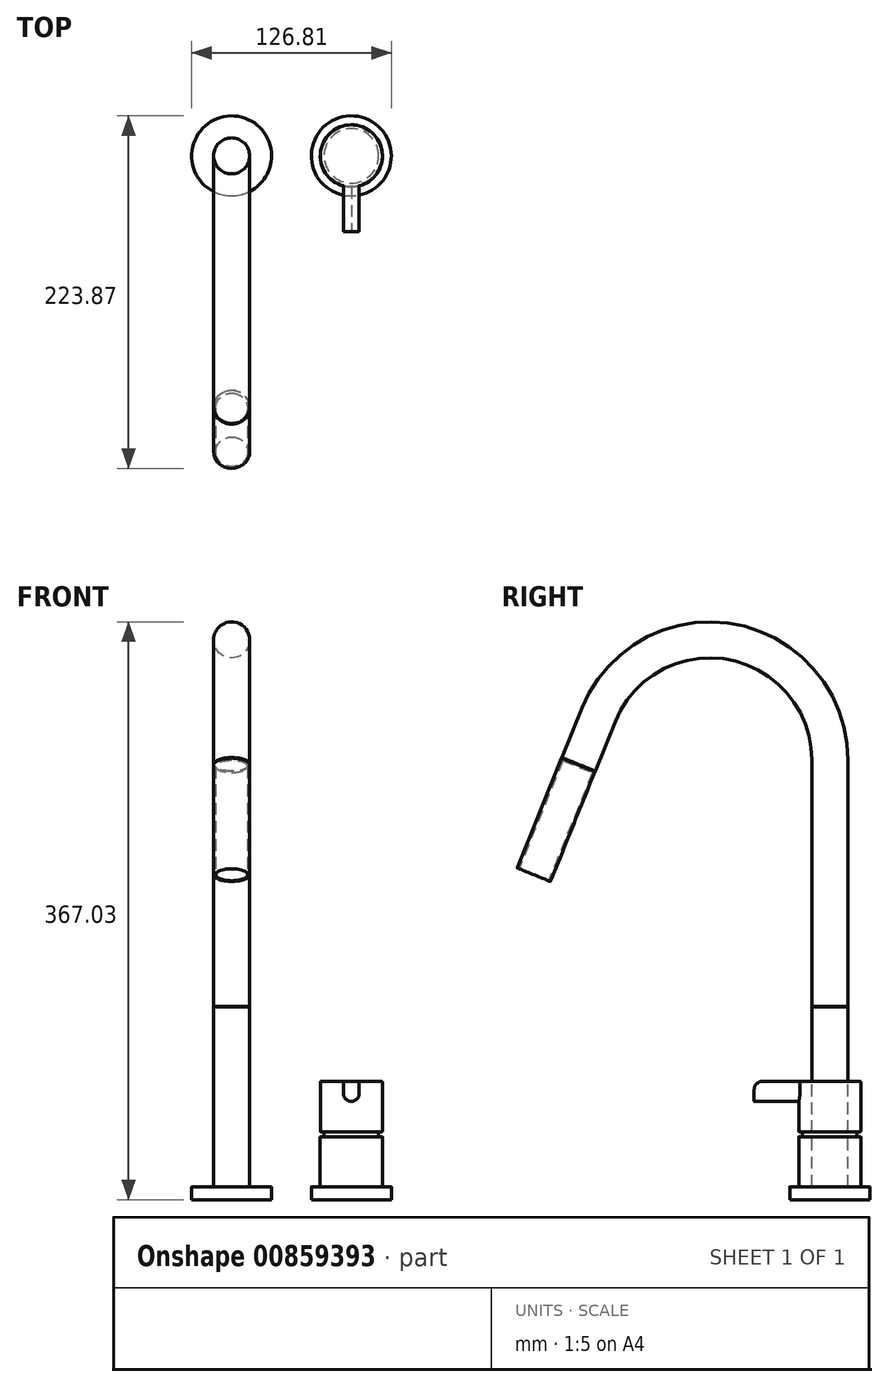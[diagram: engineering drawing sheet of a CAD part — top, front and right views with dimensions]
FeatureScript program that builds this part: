
annotation { "Feature Type Name" : "Feature", "Feature Type Description" : "" }
export const myFeature = defineFeature(function(context is Context, id is Id, definition is map)
    precondition{}
    {
        {
            var Q0;
            Q0=qCreatedBy(makeId("Top.planeOp"),FACE);
            var sketch = newSketch(context, id + "F0", { "sketchPlane" : qUnion([Q0])});
            skCircle(sketch, "E0", {"center": v(0, 0) * mm, "radius": 25.4 * mm});
            skSolve(sketch);
        }
        {
            var Q0;
            Q0=makeQuery(id+"F0.imprint","IMPRINT",FACE,{"disambiguationData":[TD([[makeQuery(id+"F0.imprint","IMPRINT",EDGE,{"derivedFrom":sQuery(id+"F0.wireOp",EDGE,"E0")}),1.0]])]});
            extrude(context, id + "F1", {"entities" : qUnion([Q0]), "depth" : 8.25 * mm, "offsetDistance" : 25.4 * mm});
        }
        {
            var Q0;
            Q0=qCreatedBy(makeId("Right.planeOp"),FACE);
            var sketch = newSketch(context, id + "F2", { "sketchPlane" : qUnion([Q0])});
            skLineSegment(sketch, "E1", {"start": v(0, 0) * mm, "end": v(0, 279.4) * mm});
            skArc(sketch, "E2", {"start": v(0, 279.4) * mm, "mid": v(-61.63, 354.2) * mm, "end": v(-146.83, 308) * mm});
            skLineSegment(sketch, "E3", {"start": v(-76.2, 279.4) * mm, "end": v(-173.41, 318.76) * mm, "construction": true});
            skLineSegment(sketch, "E4", {"start": v(-146.83, 308) * mm, "end": v(-187.97, 206.4) * mm});
            skSolve(sketch);
        }
        {
            var Q0;
            Q0=qCreatedBy(makeId("Top.planeOp"),FACE);
            var sketch = newSketch(context, id + "F3", { "sketchPlane" : qUnion([Q0])});
            skCircle(sketch, "E5", {"center": v(0, 0) * mm, "radius": 11.43 * mm});
            skSolve(sketch);
        }
        {
            var Q0;
            Q0=makeQuery(id+"F3.imprint","IMPRINT",FACE,{"disambiguationData":[TD([[makeQuery(id+"F3.imprint","IMPRINT",EDGE,{"derivedFrom":sQuery(id+"F3.wireOp",EDGE,"E5")}),1.0]])]});
            var Q1;
            Q1=sQuery(id+"F2.wireOp",EDGE,"E1");
            var Q2;
            Q2=sQuery(id+"F2.wireOp",EDGE,"E2");
            var Q3;
            Q3=sQuery(id+"F2.wireOp",EDGE,"E4");
            sweep(context, id + "F4", {"operationType" : NewBodyOperationType.ADD, "profiles" : qUnion([Q0]), "path" : qUnion([Q1, Q2, Q3])});
        }
        {
            var Q0;
            Q0=qCreatedBy(makeId("Top.planeOp"),FACE);
            var sketch = newSketch(context, id + "F5", { "sketchPlane" : qUnion([Q0])});
            skCircle(sketch, "E6", {"center": v(76.01, 0) * mm, "radius": 25.4 * mm});
            skSolve(sketch);
        }
        {
            var Q0;
            Q0 = qSketchRegion(id + "F5", true);
            extrude(context, id + "F6", {"entities" : qUnion([Q0]), "depth" : 8.25 * mm, "offsetDistance" : 25.4 * mm});
        }
        {
            var Q0;
            Q0=makeQuery(id+"F6.opExtrude","CAP_FACE",FACE,{"disambiguationData":[OSD([sQuery(id+"F5.wireOp",EDGE,"E6")])],"isStart":false});
            var sketch = newSketch(context, id + "F7", { "sketchPlane" : qUnion([Q0])});
            skCircle(sketch, "E7", {"center": v(76.01, 0) * mm, "radius": 19.74 * mm});
            skSolve(sketch);
        }
        {
            var Q0;
            Q0 = qSketchRegion(id + "F7", true);
            extrude(context, id + "F8", {"entities" : qUnion([Q0]), "operationType" : NewBodyOperationType.ADD, "depth" : 31.75 * mm, "offsetDistance" : 25.4 * mm});
        }
        {
            var Q0;
            Q0=makeQuery(id+"F8.opExtrude","CAP_FACE",FACE,{"disambiguationData":[OSD([sQuery(id+"F7.wireOp",EDGE,"E7")])],"isStart":false});
            var sketch = newSketch(context, id + "F9", { "sketchPlane" : qUnion([Q0])});
            skCircle(sketch, "E8", {"center": v(76.01, 0) * mm, "radius": 17.3 * mm});
            skSolve(sketch);
        }
        {
            var Q0;
            Q0 = qSketchRegion(id + "F9", true);
            extrude(context, id + "F10", {"entities" : qUnion([Q0]), "operationType" : NewBodyOperationType.ADD, "depth" : 3.17 * mm, "offsetDistance" : 25.4 * mm});
        }
        {
            var Q0;
            Q0=makeQuery(id+"F10.opExtrude","CAP_FACE",FACE,{"disambiguationData":[OSD([sQuery(id+"F9.wireOp",EDGE,"E8")])],"isStart":false});
            var sketch = newSketch(context, id + "F11", { "sketchPlane" : qUnion([Q0])});
            skCircle(sketch, "E9", {"center": v(76.01, 0) * mm, "radius": 19.69 * mm});
            skSolve(sketch);
        }
        {
            var Q0;
            Q0 = qSketchRegion(id + "F11", true);
            extrude(context, id + "F12", {"entities" : qUnion([Q0]), "operationType" : NewBodyOperationType.ADD, "depth" : 31.88 * mm, "offsetDistance" : 25.4 * mm});
        }
        {
            var Q0;
            Q0=makeQuery(id+"F12.opExtrude","CAP_FACE",FACE,{"disambiguationData":[OSD([sQuery(id+"F11.wireOp",EDGE,"E9")])],"isStart":false});
            var sketch = newSketch(context, id + "F13", { "sketchPlane" : qUnion([Q0])});
            skArc(sketch, "E10", {"start": v(70.99, 0) * mm, "mid": v(76.01, 5.02) * mm, "end": v(81.03, 0) * mm});
            skLineSegment(sketch, "E11", {"start": v(81.03, 0) * mm, "end": v(81.03, -48.02) * mm});
            skLineSegment(sketch, "E12", {"start": v(81.03, -48.02) * mm, "end": v(70.99, -48.02) * mm});
            skLineSegment(sketch, "E13", {"start": v(70.99, -48.02) * mm, "end": v(70.99, 0) * mm});
            skSolve(sketch);
        }
        {
            var Q0;
            Q0 = qSketchRegion(id + "F13", true);
            extrude(context, id + "F14", {"entities" : qUnion([Q0]), "operationType" : NewBodyOperationType.ADD, "oppositeDirection" : true, "depth" : 12.7 * mm, "offsetDistance" : 25.4 * mm});
        }
        {
            var Q0;
            Q0=makeQuery(id+"F14.opExtrude","CAP_EDGE",EDGE,{"disambiguationData":[OSD([sQuery(id+"F13.wireOp",EDGE,"E11")])],"isStart":false});
            var Q1;
            Q1=makeQuery(id+"F14.opExtrude","CAP_EDGE",EDGE,{"disambiguationData":[OSD([sQuery(id+"F13.wireOp",EDGE,"E13")])],"isStart":false});
            var Q2;
            Q2=makeQuery(id+"F14.opExtrude","CAP_EDGE",EDGE,{"disambiguationData":[OSD([sQuery(id+"F13.wireOp",EDGE,"E12")])],"isStart":true});
            fillet(context, id + "F15", {"entities" : qUnion([Q0, Q1, Q2]), "radius" : 5.08 * mm, "tangentPropagation" : true, "allowEdgeOverflow" : false});
        }
        {
            var Q0;
            Q0=makeQuery(id+"F6.opExtrude","CAP_EDGE",EDGE,{"disambiguationData":[OSD([sQuery(id+"F5.wireOp",EDGE,"E6")])],"isStart":false});
            var Q1;
            Q1=makeQuery(id+"F1.opExtrude","CAP_EDGE",EDGE,{"disambiguationData":[OSD([sQuery(id+"F0.wireOp",EDGE,"E0")])],"isStart":false});
            var Q2;
            Q2=makeQuery(id+"F8.opExtrude","CAP_EDGE",EDGE,{"disambiguationData":[OSD([sQuery(id+"F7.wireOp",EDGE,"E7")])],"isStart":false});
            var Q3;
            Q3=makeQuery(id+"F12.opExtrude","CAP_EDGE",EDGE,{"disambiguationData":[OSD([sQuery(id+"F11.wireOp",EDGE,"E9")])],"isStart":true});
            var Q4;
            Q4=makeQuery(id+"F12.opExtrude","CAP_EDGE",EDGE,{"disambiguationData":[OSD([sQuery(id+"F11.wireOp",EDGE,"E9")])],"isStart":false});
            var Q5;
            Q5=makeQuery(id+"F14.opExtrude","CAP_EDGE",EDGE,{"disambiguationData":[OSD([sQuery(id+"F13.wireOp",EDGE,"E13")])],"isStart":true});
            var Q6;
            Q6=makeQuery(id+"F15.opFillet","BLEND_EDGE",EDGE,{"blendedFrom":[makeQuery(id+"F14.opExtrude","CAP_EDGE",EDGE,{"disambiguationData":[OSD([sQuery(id+"F13.wireOp",EDGE,"E12")])],"isStart":true}),makeQuery(id+"F14.opExtrude","SWEPT_FACE",FACE,{"disambiguationData":[OSD([sQuery(id+"F13.wireOp",EDGE,"E11")])]})],"blendedInto":[makeQuery(id+"F14.opExtrude","SWEPT_FACE",FACE,{"disambiguationData":[OSD([sQuery(id+"F13.wireOp",EDGE,"E11")])]})]});
            var Q7;
            Q7=makeQuery(id+"F14.opExtrude","CAP_EDGE",EDGE,{"disambiguationData":[OSD([sQuery(id+"F13.wireOp",EDGE,"E11")])],"isStart":true});
            fillet(context, id + "F16", {"entities" : qUnion([Q0, Q1, Q2, Q3, Q4, Q5, Q6, Q7]), "radius" : 0.32 * mm, "tangentPropagation" : true, "allowEdgeOverflow" : false});
        }
        {
            var Q0;
            Q0=makeQuery(id+"F4.opSweep","CAP_EDGE",EDGE,{"disambiguationData":[OSD([sQuery(id+"F2.wireOp",VERTEX,"E4.end"),sQuery(id+"F3.wireOp",EDGE,"E5")])],"isStart":false});
            fillet(context, id + "F17", {"entities" : qUnion([Q0]), "radius" : 0.32 * mm, "tangentPropagation" : true, "allowEdgeOverflow" : false});
        }
        {
            var Q0;
            Q0=qCreatedBy(makeId("Right.planeOp"),FACE);
            var sketch = newSketch(context, id + "F18", { "sketchPlane" : qUnion([Q0])});
            skLineSegment(sketch, "E14.bottom", {"start": v(18.5, 122.57) * mm, "end": v(-12.47, 122.57) * mm});
            skLineSegment(sketch, "E14.top", {"start": v(18.5, 122.6) * mm, "end": v(-12.47, 122.6) * mm});
            skLineSegment(sketch, "E14.left", {"start": v(18.5, 122.6) * mm, "end": v(18.5, 122.57) * mm});
            skLineSegment(sketch, "E14.right", {"start": v(-12.47, 122.6) * mm, "end": v(-12.47, 122.57) * mm});
            skLineSegment(sketch, "E15", {"start": v(-178.29, 283.88) * mm, "end": v(-139.78, 268.41) * mm});
            skLineSegment(sketch, "E16", {"start": v(-139.78, 268.41) * mm, "end": v(-139.83, 268.3) * mm});
            skLineSegment(sketch, "E17", {"start": v(-178.33, 283.76) * mm, "end": v(-178.29, 283.88) * mm});
            skLineSegment(sketch, "E18", {"start": v(-178.33, 283.76) * mm, "end": v(-139.83, 268.3) * mm});
            skSolve(sketch);
        }
        {
            var Q0;
            Q0 = qSketchRegion(id + "F18", true);
            extrude(context, id + "F19", {"entities" : qUnion([Q0]), "operationType" : NewBodyOperationType.REMOVE, "endBound" : BoundingType.THROUGH_ALL, "oppositeDirection" : true, "depth" : 50.8 * mm, "offsetDistance" : 25.4 * mm, "hasSecondDirection" : true, "secondDirectionBound" : SecondDirectionBoundingType.THROUGH_ALL, "secondDirectionOppositeDirection" : false, "secondDirectionDepth" : 25.4 * mm});
        }
        {
            var Q0;
            Q0=makeQuery(id+"F4.opSweep","CAP_FACE",FACE,{"disambiguationData":[OSD([sQuery(id+"F2.wireOp",VERTEX,"E4.end"),sQuery(id+"F3.wireOp",EDGE,"E5")])],"isStart":false});
            shell(context, id + "F20", {"entities" : qUnion([Q0]), "thickness" : 1.27 * mm});
        }
        {
            var Q0;
            Q0=makeQuery(id+"F19.boolean.opBoolean","INTERSECT",EDGE,{"derivedFrom":[makeQuery(id+"F4.opSweep","SWEPT_FACE",FACE,{"disambiguationData":[OSD([sQuery(id+"F2.wireOp",EDGE,"E4"),sQuery(id+"F3.wireOp",EDGE,"E5")])]}),makeQuery(id+"F19.opExtrude","SWEPT_FACE",FACE,{"disambiguationData":[OSD([sQuery(id+"F18.wireOp",EDGE,"E15")])]})]});
            var Q1;
            Q1=makeQuery(id+"F19.boolean.opBoolean","INTERSECT",EDGE,{"derivedFrom":[makeQuery(id+"F4.opSweep","SWEPT_FACE",FACE,{"disambiguationData":[OSD([sQuery(id+"F2.wireOp",EDGE,"E4"),sQuery(id+"F3.wireOp",EDGE,"E5")])]}),makeQuery(id+"F19.opExtrude","SWEPT_FACE",FACE,{"disambiguationData":[OSD([sQuery(id+"F18.wireOp",EDGE,"E18")])]})]});
            var Q2;
            Q2=makeQuery(id+"F19.boolean.opBoolean","INTERSECT",EDGE,{"derivedFrom":[makeQuery(id+"F4.opSweep","SWEPT_FACE",FACE,{"disambiguationData":[OSD([sQuery(id+"F2.wireOp",EDGE,"E1"),sQuery(id+"F3.wireOp",EDGE,"E5")])]}),makeQuery(id+"F19.opExtrude","SWEPT_FACE",FACE,{"disambiguationData":[OSD([sQuery(id+"F18.wireOp",EDGE,"E14.bottom")])]})]});
            var Q3;
            Q3=makeQuery(id+"F19.boolean.opBoolean","INTERSECT",EDGE,{"derivedFrom":[makeQuery(id+"F4.opSweep","SWEPT_FACE",FACE,{"disambiguationData":[OSD([sQuery(id+"F2.wireOp",EDGE,"E1"),sQuery(id+"F3.wireOp",EDGE,"E5")])]}),makeQuery(id+"F19.opExtrude","SWEPT_FACE",FACE,{"disambiguationData":[OSD([sQuery(id+"F18.wireOp",EDGE,"E14.top")])]})]});
            fillet(context, id + "F21", {"entities" : qUnion([Q0, Q1, Q2, Q3]), "radius" : 0.13 * mm, "tangentPropagation" : true, "allowEdgeOverflow" : false});
        }
    });
